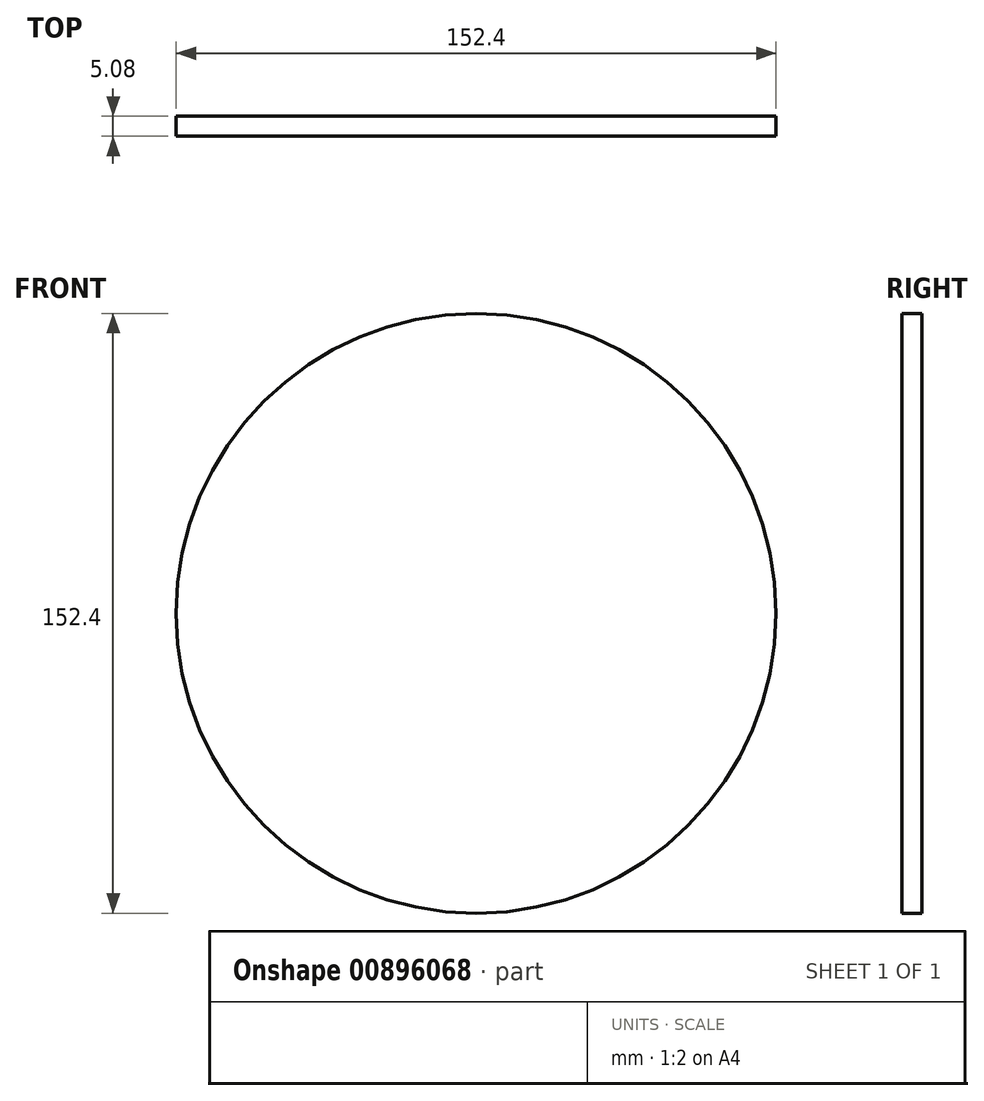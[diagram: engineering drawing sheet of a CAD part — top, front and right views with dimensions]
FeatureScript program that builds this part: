
annotation { "Feature Type Name" : "Feature", "Feature Type Description" : "" }
export const myFeature = defineFeature(function(context is Context, id is Id, definition is map)
    precondition{}
    {
        {
            var Q0;
            Q0=qCreatedBy(makeId("Front.planeOp"),FACE);
            var sketch = newSketch(context, id + "F0", { "sketchPlane" : qUnion([Q0])});
            skCircle(sketch, "E0", {"center": v(0, 0) * mm, "radius": 76.2 * mm});
            skSolve(sketch);
        }
        {
            var Q0;
            Q0=makeQuery(id+"F0.imprint","IMPRINT",FACE,{"disambiguationData":[TD([[makeQuery(id+"F0.imprint","IMPRINT",EDGE,{"derivedFrom":sQuery(id+"F0.wireOp",EDGE,"E0")}),1.0]])]});
            extrude(context, id + "F1", {"entities" : qUnion([Q0]), "depth" : 5.08 * mm, "offsetDistance" : 25.4 * mm});
        }
    });
